# Revit family: Gira_109103
name_source: partatom
category: Electrical Fixtures
revit_build: Autodesk Revit 2017 (Build: 20160225_1515(x64)
units: mm (PartAtom-declared; Revit-internal decimal feet)

## family parameters
Cut with Voids When Loaded = No
Host = Face
Maintain Annotation Orientation = No
Part Type = Normal
Room Calculation Point = No
Round Connector Dimension = Use Diameter
Shared = No

## types (1)
- Gira_109103
    Anzahl der Einheiten = 1
    Anzahl der Einheiten vertikal = 1
    Ausführung der Oberfläche = glänzend
    BIM = https://media.stage.bim.site
    Befestigungsart = Klemmbefestigung
    Datenblatt = https://katalog.gira.de
    Default Elevation = 1219 mm
    Description = Abdeckrahmen Gira Standard 55 mit Beschriftungsfeld Reinweiß glänzend 1fach Merkmale: - Bruchsicher. - Sprühnebeldicht. - Abdeckrahmen mit transparentem Sichtfenster zur Beschriftung der Einsätze. - Besonders geeignet für Objekte, in denen Elektroinstallation gekennzeichnet und dokumentiert werden muss, bspw. in Verwaltungen, gewerblichen Betrieben, Flughäfen, Unternehmen und Krankenhäusern.  Hinweise : - Nicht zu verwenden mit: Dichtungsset IP44, Aufputz-Gehäuse flache Bauweise, Aufputz-Gehäuse.
    Farbe = weiß
    GTIN = 4010337091035
    Geeignet für Einbauinstallation = No
    Geeignet für Geräteeinbaukanal = No
    Geeignet für Unterflurkanaldose = No
    Geeignet für Unterputz-Installation = Yes
    HAN = 109103
    Halogenfrei = Yes
    Keynote = Std55_Rahmen_1fach
    Manufacturer = Gira
    Mit Klappdeckel = No
    Mit Montagerahmen = No
    Montagerichtung = vertikal
    Oberfläche = sonstige
    Produktseite = http://katalog.gira.de
    RAL-Nummer (ähnlich) = 9010
    Schutzart (IP) = IP20
    Textfeld/Beschriftungsfläche = Yes
    Transparent = No
    Typname = Abdeckrahmen 1f BSF Gira E2 Reinweiß
    URL = https://www.gira.de
    Werkstoff = Kunststoff
    Werkstoffgüte = Thermoplast

## geometry (parser evidence)
native form markers: Blend x2, Sweep x3
no freeform markers — native parametric forms only
